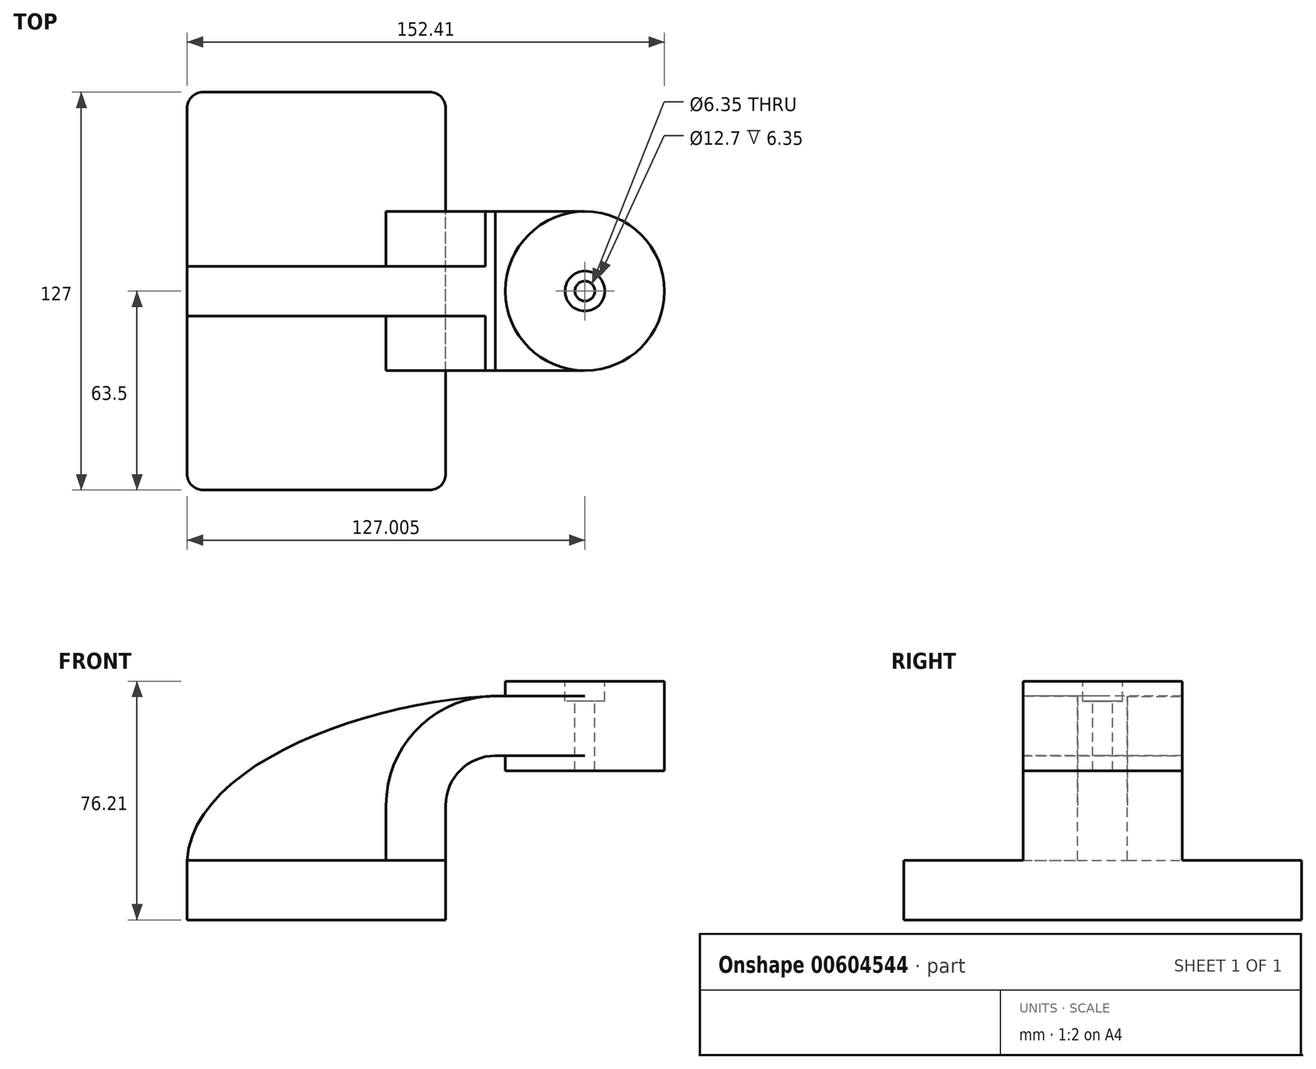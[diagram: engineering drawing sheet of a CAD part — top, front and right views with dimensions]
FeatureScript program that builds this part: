
annotation { "Feature Type Name" : "Feature", "Feature Type Description" : "" }
export const myFeature = defineFeature(function(context is Context, id is Id, definition is map)
    precondition{}
    {
        {
            var Q0;
            Q0=qCreatedBy(makeId("Front.planeOp"),FACE);
            var sketch = newSketch(context, id + "F0", { "sketchPlane" : qUnion([Q0])});
            skLineSegment(sketch, "E0.rect.bottom", {"start": v(-41.28, 9.52) * mm, "end": v(41.28, 9.52) * mm});
            skLineSegment(sketch, "E0.rect.top", {"start": v(-41.28, -9.52) * mm, "end": v(41.28, -9.52) * mm});
            skLineSegment(sketch, "E0.rect.left", {"start": v(-41.28, 9.52) * mm, "end": v(-41.28, -9.52) * mm});
            skLineSegment(sketch, "E0.rect.right", {"start": v(41.28, 9.52) * mm, "end": v(41.28, -9.52) * mm});
            skPoint(sketch, "E0.rect.middle", {"position": v(0, 0) * mm});
            skLineSegment(sketch, "E1", {"start": v(41.28, 9.52) * mm, "end": v(41.28, 27) * mm});
            skArc(sketch, "E2", {"start": v(41.28, 27) * mm, "mid": v(45.92, 38.23) * mm, "end": v(57.15, 42.88) * mm});
            skLineSegment(sketch, "E3", {"start": v(57.15, 42.88) * mm, "end": v(85.72, 42.88) * mm});
            skLineSegment(sketch, "E4.rect.bottom", {"start": v(60.32, 38.1) * mm, "end": v(111.12, 38.1) * mm});
            skLineSegment(sketch, "E4.rect.top", {"start": v(60.32, 66.68) * mm, "end": v(111.12, 66.68) * mm});
            skLineSegment(sketch, "E4.rect.left", {"start": v(60.32, 38.1) * mm, "end": v(60.32, 66.68) * mm});
            skLineSegment(sketch, "E4.rect.right", {"start": v(111.13, 38.1) * mm, "end": v(111.12, 66.68) * mm});
            skPoint(sketch, "E4.rect.middle", {"position": v(85.72, 52.39) * mm});
            skLineSegment(sketch, "E5.0", {"start": v(57.15, 61.93) * mm, "end": v(85.72, 61.93) * mm});
            skArc(sketch, "E5.1", {"start": v(22.23, 27) * mm, "mid": v(32.45, 51.7) * mm, "end": v(57.15, 61.93) * mm});
            skLineSegment(sketch, "E5.2", {"start": v(22.23, 9.52) * mm, "end": v(22.23, 27) * mm});
            skLineSegment(sketch, "E6", {"start": v(85.72, 38.1) * mm, "end": v(85.72, 66.68) * mm});
            skFitSpline(sketch, "E7", {"points": [v(-41.28, 9.53) * mm, v(57.15, 61.93) * mm], "startDerivative": vector(5.2, 92.34) * mm, "endDerivative": vector(120.92, 4.22) * mm});
            skSolve(sketch);
        }
        {
            var Q0;
            Q0=makeQuery(id+"F0.imprint","IMPRINT",FACE,{"disambiguationData":[TD([[makeQuery(id+"F0.imprint","IMPRINT",EDGE,{"derivedFrom":sQuery(id+"F0.wireOp",EDGE,"E0.rect.top")}),1.0]])]});
            extrude(context, id + "F1", {"entities" : qUnion([Q0]), "endBound" : BoundingType.SYMMETRIC, "depth" : 127 * mm});
        }
        {
            var Q0;
            {var subQ9=sQuery(id+"F0.wireOp",EDGE,"E1");Q0=makeQuery(id+"F0.imprint","IMPRINT",FACE,{"disambiguationData":[TD([[makeQuery(id+"F0.imprint","IMPRINT",EDGE,{"derivedFrom":subQ9}),1.0]])]});}
            var Q1;
            {var subQ0=sQuery(id+"F0.wireOp",EDGE,"E6");var subQ1=sQuery(id+"F0.wireOp",EDGE,"E3");var subQ2=makeQuery(id+"F0.imprint","INTERSECT",VERTEX,{"derivedFrom":[subQ1,subQ0]});Q1=makeQuery(id+"F0.imprint","IMPRINT",FACE,{"disambiguationData":[TD([[makeQuery(id+"F0.imprint","IMPRINT",EDGE,{"disambiguationData":[TD([[subQ2,1.0]])],"derivedFrom":subQ1}),1.0]])]});}
            extrude(context, id + "F2", {"entities" : qUnion([Q0, Q1]), "operationType" : NewBodyOperationType.ADD, "endBound" : BoundingType.SYMMETRIC, "depth" : 50.8 * mm});
        }
        {
            var Q0;
            {var subQ3=sQuery(id+"F0.wireOp",EDGE,"E5.2");Q0=makeQuery(id+"F0.imprint","IMPRINT",FACE,{"disambiguationData":[TD([[makeQuery(id+"F0.imprint","IMPRINT",EDGE,{"derivedFrom":subQ3}),1.0]])]});}
            extrude(context, id + "F3", {"entities" : qUnion([Q0]), "operationType" : NewBodyOperationType.ADD, "endBound" : BoundingType.SYMMETRIC, "depth" : 15.88 * mm});
        }
        {
            var Q0;
            {var subQ5=sQuery(id+"F0.wireOp",EDGE,"E4.rect.right");Q0=makeQuery(id+"F0.imprint","IMPRINT",FACE,{"disambiguationData":[TD([[makeQuery(id+"F0.imprint","IMPRINT",EDGE,{"derivedFrom":subQ5}),1.0]])]});}
            var Q1;
            Q1=sQuery(id+"F0.wireOp",EDGE,"E6");
            revolve(context, id + "F4", {"operationType" : NewBodyOperationType.ADD, "entities" : qUnion([Q0]), "axis" : qUnion([Q1]), "revolveType" : RevolveType.FULL});
        }
        {
            var Q0;
            Q0=makeQuery(id+"F1.opExtrude","CAP_EDGE",EDGE,{"disambiguationData":[OSD([sQuery(id+"F0.wireOp",EDGE,"E0.rect.right")])],"isStart":false});
            var Q1;
            Q1=makeQuery(id+"F1.opExtrude","CAP_EDGE",EDGE,{"disambiguationData":[OSD([sQuery(id+"F0.wireOp",EDGE,"E0.rect.left")])],"isStart":false});
            var Q2;
            Q2=makeQuery(id+"F1.opExtrude","CAP_EDGE",EDGE,{"disambiguationData":[OSD([sQuery(id+"F0.wireOp",EDGE,"E0.rect.right")])],"isStart":true});
            var Q3;
            Q3=makeQuery(id+"F1.opExtrude","CAP_EDGE",EDGE,{"disambiguationData":[OSD([sQuery(id+"F0.wireOp",EDGE,"E0.rect.left")])],"isStart":true});
            fillet(context, id + "F5", {"entities" : qUnion([Q0, Q1, Q2, Q3]), "radius" : 5.08 * mm, "tangentPropagation" : true, "allowEdgeOverflow" : false});
        }
        {
            var Q0;
            Q0=makeQuery(id+"F4.opRevolve","SWEPT_FACE",FACE,{"disambiguationData":[OSD([sQuery(id+"F0.wireOp",EDGE,"E4.rect.top")])]});
            var sketch = newSketch(context, id + "F6", { "sketchPlane" : qUnion([Q0])});
            skCircle(sketch, "E8", {"center": v(85.72, 0) * mm, "radius": 4.98 * mm});
            skSolve(sketch);
        }
        {
            var Q0;
            Q0=sQuery(id+"F6.wireOp",VERTEX,"E8.center");
            var Q1;
            Q1=makeQuery(id+"F1.opExtrude","SWEPT_BODY",BODY,{"disambiguationData":[OSD([sQuery(id+"F0.wireOp",EDGE,"E0.rect.bottom"),sQuery(id+"F0.wireOp",EDGE,"E0.rect.top"),sQuery(id+"F0.wireOp",EDGE,"E0.rect.left"),sQuery(id+"F0.wireOp",EDGE,"E0.rect.right")])]});
            hole(context, id + "F7", {"style" : HoleStyle.C_BORE, "endStyle" : HoleEndStyle.THROUGH, "holeDiameter" : 6.35 * mm, "cBoreDiameter" : 12.7 * mm, "cBoreDepth" : 6.35 * mm, "majorDiameter" : 6.35 * mm, "isTappedThrough" : true, "tappedDepth" : 12.7 * mm, "tapClearance" : 3, "startFromSketch" : true, "locations" : qUnion([Q0]), "scope" : qUnion([Q1])});
        }
    });
